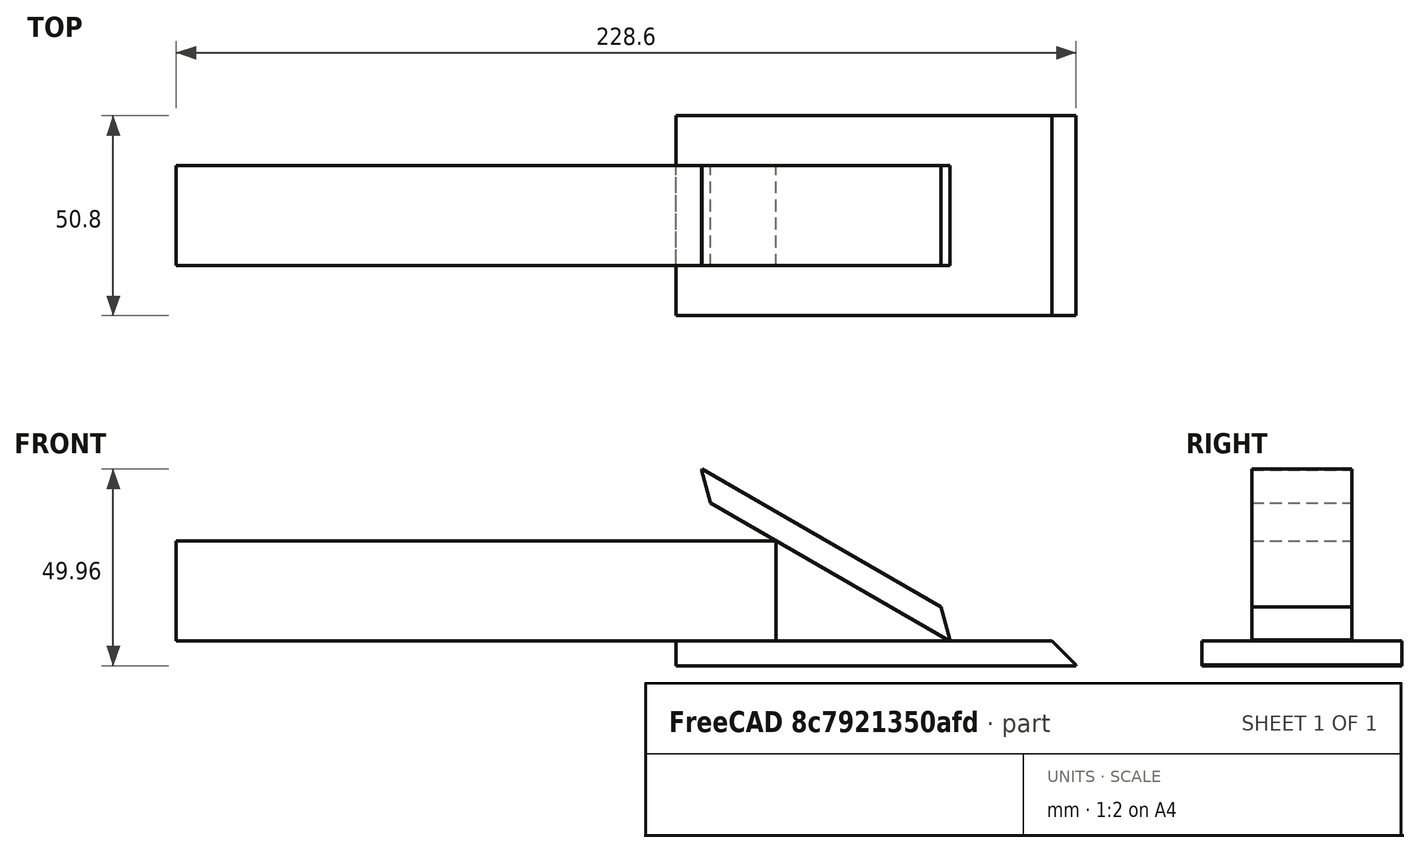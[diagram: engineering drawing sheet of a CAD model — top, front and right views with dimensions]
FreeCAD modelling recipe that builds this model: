
FCSTD DOCUMENT  (FreeCAD 0.16R6712 (Git))
Label: LT_Tooth bar
License: All rights reserved
LicenseURL: http://en.wikipedia.org/wiki/All_rights_reserved
objects: Part::Box×3, Part::Chamfer×2, Part::MultiFuse×1
note: 6 computed .brp shape members not serialized (recipe doc carries the construction recipe); baked Part::Feature solids carry a one-line shape summary decoded from their .brp

FEATURE [Part::Box] Box  label="Shaft"
  Height = 25.4
  Length = 152.4
  Width = 25.4
FEATURE [Part::Box] Box001  label="Cube"
  Height = 6.35
  Length = 101.6
  Placement = pos=(127,-12.7,-6.35) rot=(0,0,1;0rad)
  Width = 50.8
FEATURE [Part::Box] Box002  label="Cube 01"
  Height = 6.35
  Length = 76.2
  Placement = pos=(130.39,-0.875268,38.108) rot=(0,1,0;0.523599rad)
  Width = 25.4
FEATURE [Part::Chamfer] Chamfer  label="Knife"
  Base = -> Box001
  Edges = 1 edges r=6.1: [Edge6]
FEATURE [Part::Chamfer] Chamfer001  label="Breaker bar"
  Base = -> Box002
  Edges = 2 edges r=6.1: [Edge4,Edge6]
  Placement = pos=(0,0.875268,0) rot=(0,0,1;0rad)
FEATURE [Part::MultiFuse] Fusion  label="Tooth Bar"
  Shapes = -> [Box,Chamfer001,Chamfer]
